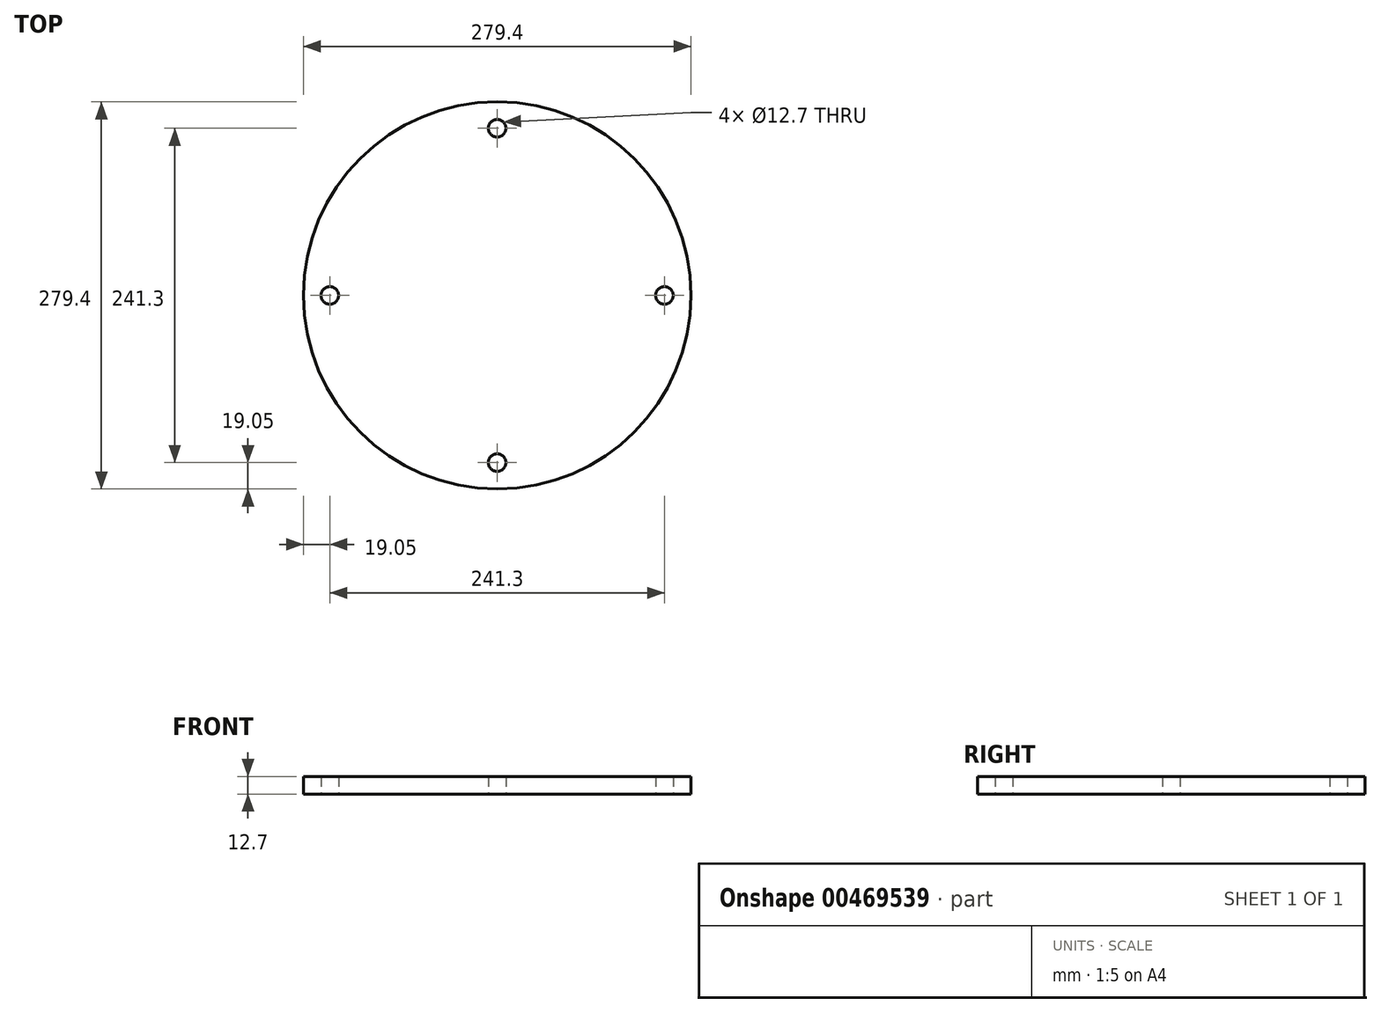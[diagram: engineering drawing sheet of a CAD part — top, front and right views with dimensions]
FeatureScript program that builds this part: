
annotation { "Feature Type Name" : "Feature", "Feature Type Description" : "" }
export const myFeature = defineFeature(function(context is Context, id is Id, definition is map)
    precondition{}
    {
        {
            var Q0;
            Q0=qCreatedBy(makeId("Top.planeOp"),FACE);
            var sketch = newSketch(context, id + "F0", { "sketchPlane" : qUnion([Q0])});
            skCircle(sketch, "E0", {"center": v(0, 0) * mm, "radius": 139.7 * mm});
            skCircle(sketch, "E1", {"center": v(0, 0) * mm, "radius": 120.65 * mm, "construction": true});
            skCircle(sketch, "E2", {"center": v(120.65, 0) * mm, "radius": 6.35 * mm});
            skCircle(sketch, "E3.1.0", {"center": v(0, 120.65) * mm, "radius": 6.35 * mm});
            skCircle(sketch, "E3.2.0", {"center": v(-120.65, 0) * mm, "radius": 6.35 * mm});
            skCircle(sketch, "E3.3.0", {"center": v(0, -120.65) * mm, "radius": 6.35 * mm});
            skSolve(sketch);
        }
        {
            var Q0;
            Q0 = qSketchRegion(id + "F0", true);
            extrude(context, id + "F1", {"entities" : qUnion([Q0]), "depth" : 12.7 * mm, "offsetDistance" : 25.4 * mm});
        }
    });
